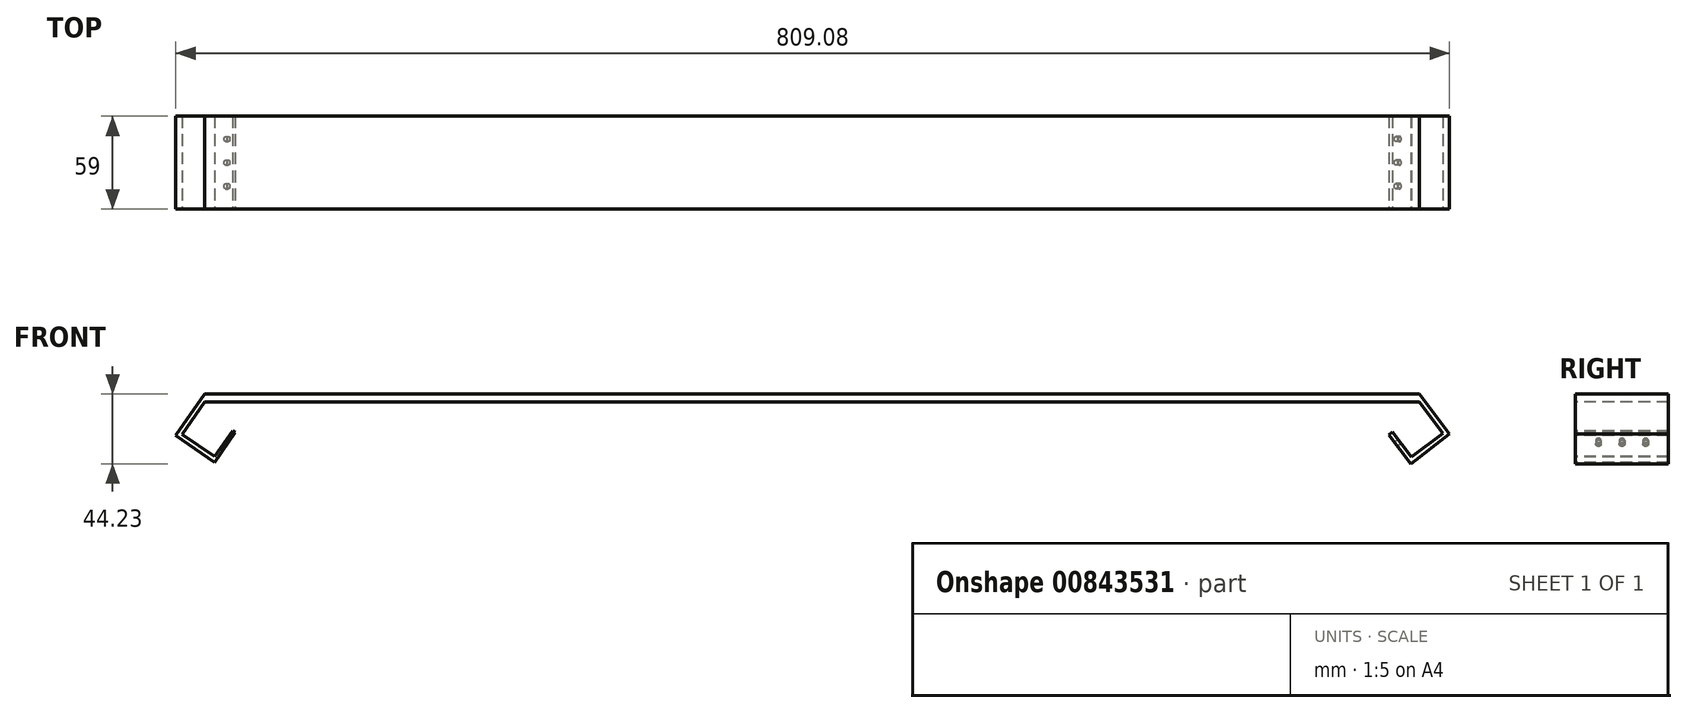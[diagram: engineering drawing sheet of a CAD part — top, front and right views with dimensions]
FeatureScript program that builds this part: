
annotation { "Feature Type Name" : "Feature", "Feature Type Description" : "" }
export const myFeature = defineFeature(function(context is Context, id is Id, definition is map)
    precondition{}
    {
        {
            var Q0;
            Q0=qCreatedBy(makeId("Front.planeOp"),FACE);
            var sketch = newSketch(context, id + "F0", { "sketchPlane" : qUnion([Q0])});
            skLineSegment(sketch, "E0.bottom", {"start": v(385.75, 2.5) * mm, "end": v(-385.75, 2.5) * mm});
            skLineSegment(sketch, "E0.top", {"start": v(385.75, -2.5) * mm, "end": v(-385.75, -2.5) * mm});
            skLineSegment(sketch, "E0.left", {"start": v(385.75, 2.5) * mm, "end": v(385.75, -2.5) * mm});
            skLineSegment(sketch, "E0.right", {"start": v(-385.75, 2.5) * mm, "end": v(-385.75, -2.5) * mm});
            skPoint(sketch, "E0.middle", {"position": v(0, 0) * mm});
            skLineSegment(sketch, "E1", {"start": v(-385.75, 2.5) * mm, "end": v(-402.28, -21.47) * mm});
            skLineSegment(sketch, "E2", {"start": v(-402.28, -21.47) * mm, "end": v(-399.95, -23.08) * mm});
            skLineSegment(sketch, "E3", {"start": v(-399.95, -23.08) * mm, "end": v(-385.75, -2.5) * mm});
            skLineSegment(sketch, "E4", {"start": v(-402.28, -21.47) * mm, "end": v(-403.99, -23.94) * mm});
            skLineSegment(sketch, "E5", {"start": v(-403.99, -23.94) * mm, "end": v(-381.07, -39.74) * mm});
            skLineSegment(sketch, "E6", {"start": v(-381.07, -39.74) * mm, "end": v(-379.37, -37.27) * mm});
            skLineSegment(sketch, "E7", {"start": v(-379.37, -37.27) * mm, "end": v(-402.28, -21.47) * mm});
            skLineSegment(sketch, "E8", {"start": v(385.75, 2.5) * mm, "end": v(403.27, -20.59) * mm});
            skLineSegment(sketch, "E9", {"start": v(403.27, -20.59) * mm, "end": v(400.86, -22.41) * mm});
            skLineSegment(sketch, "E10", {"start": v(400.86, -22.41) * mm, "end": v(385.75, -2.5) * mm});
            skLineSegment(sketch, "E11", {"start": v(403.27, -20.59) * mm, "end": v(405.09, -22.98) * mm});
            skLineSegment(sketch, "E12", {"start": v(405.09, -22.98) * mm, "end": v(382.77, -39.92) * mm});
            skLineSegment(sketch, "E13", {"start": v(382.77, -39.92) * mm, "end": v(380.95, -37.53) * mm});
            skLineSegment(sketch, "E14", {"start": v(380.95, -37.53) * mm, "end": v(400.86, -22.41) * mm});
            skLineSegment(sketch, "E15", {"start": v(-381.07, -39.74) * mm, "end": v(-368.01, -20.81) * mm});
            skLineSegment(sketch, "E16", {"start": v(-368.01, -20.81) * mm, "end": v(-366.3, -21.99) * mm});
            skLineSegment(sketch, "E17", {"start": v(-366.3, -21.99) * mm, "end": v(-379.37, -40.92) * mm});
            skLineSegment(sketch, "E18", {"start": v(-379.37, -40.92) * mm, "end": v(-381.07, -39.74) * mm});
            skLineSegment(sketch, "E19", {"start": v(382.77, -39.92) * mm, "end": v(368.86, -21.6) * mm});
            skLineSegment(sketch, "E20", {"start": v(368.86, -21.6) * mm, "end": v(366.47, -23.41) * mm});
            skLineSegment(sketch, "E21", {"start": v(366.47, -23.41) * mm, "end": v(380.38, -41.73) * mm});
            skLineSegment(sketch, "E22", {"start": v(380.38, -41.73) * mm, "end": v(382.77, -39.92) * mm});
            skSolve(sketch);
        }
        {
            var Q0;
            Q0=qSketchRegion(id+"F0",true);
            extrude(context, id + "F1", {"entities" : qUnion([Q0]), "oppositeDirection" : true, "depth" : 59 * mm, "offsetDistance" : 25 * mm, "symmetric" : true});
        }
        {
            var Q0;
            Q0=makeQuery(id+"F1.opExtrude","SWEPT_FACE",FACE,{"disambiguationData":[OSD([sQuery(id+"F0.wireOp",EDGE,"E17")])]});
            var sketch = newSketch(context, id + "F2", { "sketchPlane" : qUnion([Q0])});
            skLineSegment(sketch, "E23", {"start": v(-14.75, -233.6) * mm, "end": v(14.75, -233.6) * mm, "construction": true});
            skCircle(sketch, "E24", {"center": v(-15, -233.6) * mm, "radius": 1.65 * mm});
            skCircle(sketch, "E25", {"center": v(0, -233.6) * mm, "radius": 1.65 * mm});
            skCircle(sketch, "E26", {"center": v(15, -233.6) * mm, "radius": 1.65 * mm});
            skSolve(sketch);
        }
        {
            var Q0;
            Q0=qSketchRegion(id+"F2",true);
            extrude(context, id + "F3", {"entities" : qUnion([Q0]), "operationType" : NewBodyOperationType.REMOVE, "oppositeDirection" : true, "depth" : 3 * mm, "offsetDistance" : 25 * mm});
        }
        {
            var Q0;
            Q0=makeQuery(id+"F1.opExtrude","SWEPT_FACE",FACE,{"disambiguationData":[OSD([sQuery(id+"F0.wireOp",EDGE,"E21")])]});
            var sketch = newSketch(context, id + "F4", { "sketchPlane" : qUnion([Q0])});
            skLineSegment(sketch, "E27", {"start": v(-14.75, -247.72) * mm, "end": v(14.75, -247.72) * mm, "construction": true});
            skCircle(sketch, "E28", {"center": v(0, -247.72) * mm, "radius": 1.65 * mm});
            skCircle(sketch, "E29", {"center": v(-15, -247.72) * mm, "radius": 1.65 * mm});
            skCircle(sketch, "E30", {"center": v(15, -247.72) * mm, "radius": 1.65 * mm});
            skSolve(sketch);
        }
        {
            var Q0;
            Q0=qSketchRegion(id+"F4",true);
            extrude(context, id + "F5", {"entities" : qUnion([Q0]), "operationType" : NewBodyOperationType.REMOVE, "oppositeDirection" : true, "depth" : 25 * mm, "offsetDistance" : 25 * mm});
        }
    });
